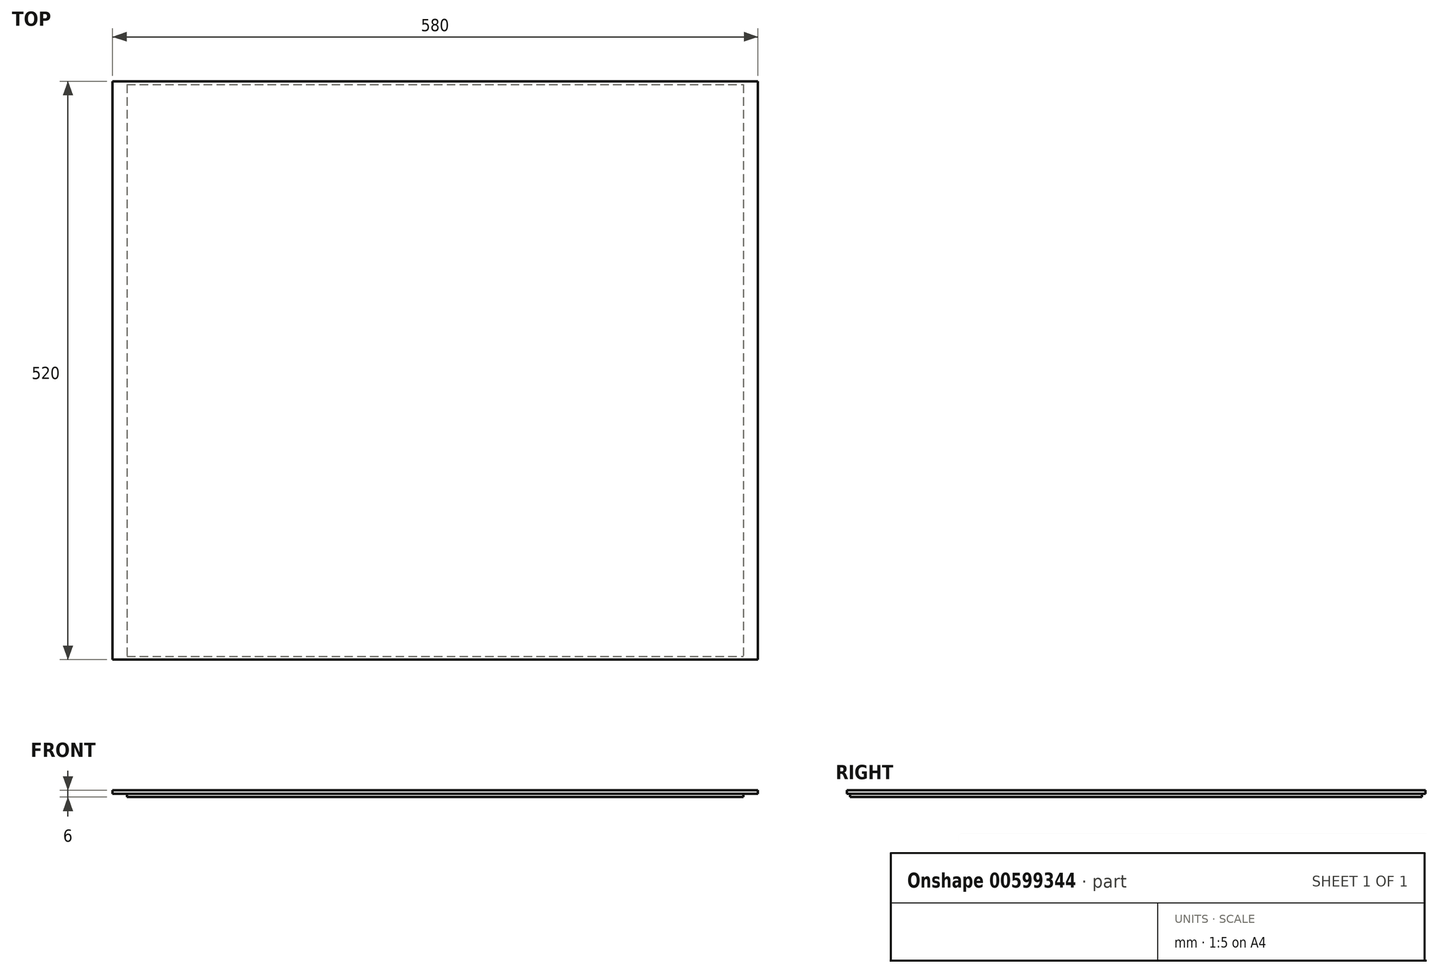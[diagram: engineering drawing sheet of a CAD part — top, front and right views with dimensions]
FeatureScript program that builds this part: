
annotation { "Feature Type Name" : "Feature", "Feature Type Description" : "" }
export const myFeature = defineFeature(function(context is Context, id is Id, definition is map)
    precondition{}
    {
        {
            var Q0;
            Q0=qCreatedBy(makeId("Top.planeOp"),FACE);
            var sketch = newSketch(context, id + "F0", { "sketchPlane" : qUnion([Q0])});
            skLineSegment(sketch, "E0.bottom", {"start": v(-277, 257) * mm, "end": v(277, 257) * mm});
            skLineSegment(sketch, "E0.top", {"start": v(-277, -257) * mm, "end": v(277, -257) * mm});
            skLineSegment(sketch, "E0.left", {"start": v(-277, 257) * mm, "end": v(-277, -257) * mm});
            skLineSegment(sketch, "E0.right", {"start": v(277, 257) * mm, "end": v(277, -257) * mm});
            skSolve(sketch);
        }
        {
            var Q0;
            Q0=qSketchRegion(id+"F0",true);
            extrude(context, id + "F1", {"entities" : qUnion([Q0]), "depth" : 3 * mm});
        }
        {
            var Q0;
            Q0=makeQuery(id+"F1.opExtrude","CAP_FACE",FACE,{"disambiguationData":[OSD([sQuery(id+"F0.wireOp",EDGE,"E0.bottom"),sQuery(id+"F0.wireOp",EDGE,"E0.top"),sQuery(id+"F0.wireOp",EDGE,"E0.left"),sQuery(id+"F0.wireOp",EDGE,"E0.right")])],"isStart":false});
            var sketch = newSketch(context, id + "F2", { "sketchPlane" : qUnion([Q0])});
            skLineSegment(sketch, "E1.bottom", {"start": v(-280, 260) * mm, "end": v(280, 260) * mm});
            skLineSegment(sketch, "E1.top", {"start": v(-280, -260) * mm, "end": v(280, -260) * mm});
            skLineSegment(sketch, "E1.left", {"start": v(-280, 260) * mm, "end": v(-280, -260) * mm});
            skLineSegment(sketch, "E1.right", {"start": v(280, 260) * mm, "end": v(280, -260) * mm});
            skLineSegment(sketch, "E2.bottom", {"start": v(-280, 260) * mm, "end": v(-290, 260) * mm});
            skLineSegment(sketch, "E2.top", {"start": v(-280, -260) * mm, "end": v(-290, -260) * mm});
            skLineSegment(sketch, "E2.right", {"start": v(-290, 260) * mm, "end": v(-290, -260) * mm});
            skLineSegment(sketch, "E3.bottom", {"start": v(280, -260) * mm, "end": v(290, -260) * mm});
            skLineSegment(sketch, "E3.top", {"start": v(280, 260) * mm, "end": v(290, 260) * mm});
            skLineSegment(sketch, "E3.left", {"start": v(280, -260) * mm, "end": v(280, 260) * mm});
            skLineSegment(sketch, "E3.right", {"start": v(290, -260) * mm, "end": v(290, 260) * mm});
            skSolve(sketch);
        }
        {
            var Q0;
            Q0=qSketchRegion(id+"F2",true);
            extrude(context, id + "F3", {"entities" : qUnion([Q0]), "depth" : 3 * mm});
        }
    });
